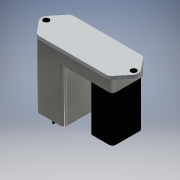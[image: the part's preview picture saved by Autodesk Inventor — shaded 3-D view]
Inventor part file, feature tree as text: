
AUTODESK INVENTOR PART (.ipt)
format: ipt  version: 2018 (Build 220112000, 112)  size: 233,984 bytes
history: native  units: mm
features: sketch x6, extrude x5, hole x1
ambient origin geometry x8: Origin, YZ Plane, XZ Plane, XY Plane, X Axis, Y Axis, Z Axis, Center Point
bodies: Volumenkörper1 (feature_tree)
feature tree (12):
  extrude  "Extrusion1"  Depth=12.0mm
  hole  "Bohrung1"  [1 undecoded]
  extrude  "Extrusion2"  Depth=2.0mm
  extrude  "Extrusion3"  Depth=67.0mm
  extrude  "Extrusion4"  Depth=3.1mm
  extrude  "Extrusion5"  Depth=25.0mm
  sketch  "Skizze1"  dims[d2=12.0mm d3=12.0mm]
  sketch  "Skizze2"  dims[d6=4.5mm d7=2.8mm d8=0.0mm]
  sketch  "Skizze3"  dims[d9=75.5mm d10=2.0mm]
  sketch  "Skizze4"  dims[d11=3.2mm d12=6.0mm d13=5.0mm d14=2.0mm d15=90.0deg d16=8.0mm d17=20.594885mm d20=67.0mm]
  sketch  "Skizze5"  dims[d21=4.25mm d22=3.1mm]
  sketch  "Skizze6"  dims[d23=10.0mm d24=0.0mm d25=25.0mm d26=3.1mm d27=0.0mm d28=3.1mm d29=46.0mm d30=0.0mm d31=0.4mm d33=0.8mm d35=4.8mm d37=11.6mm d38=8.0mm d39=0.0mm d40=20.0mm d41=3.1mm d42=40.2mm d43=0.0mm d44=28.2mm d45=0.9mm d46=0.9mm d47=71.5mm d48=21.0mm d49=21.0mm d50=58.0mm d51=58.0mm d52=15.0mm d53=15.0mm d54=8.791223mm d55=8.791223mm d56=8.788764mm d57=8.788764mm d58=0.9mm d59=0.9mm d60=0.9mm d61=26.4mm d62=0.8mm d63=0.8mm d64=4.8mm d65=4.8mm d66=6.0mm d67=6.0mm d68=0.0mm d69=9.0mm]
note: 1 required parameter value undecoded (feature->parameter linkage not recoverable at this tier; creation-order binding heuristic only, values carry confidence <= 0.55)
